# Revit family: STS-504_RV17_LOD400 (05.11.23)
name_source: partatom
category: Электрооборудование
revit_build: Autodesk Revit 2017 (Build: 20170118_1100(x64)
units: mm (PartAtom-declared; Revit-internal decimal feet)

## family parameters
Всегда вертикально = Да
Конфигурация панели = Два столбца, слева направо
На основе рабочей плоскости = Нет
Общий = Нет
При загрузке вырезать с полостями = Нет
Размер круглого соединителя = Использовать диаметр
Тип детали = Щит
Точка расчета площади = Нет

## types (1)
- STS-504
    ADSK_URL страницы изделия = https://stilsoft.ru
    ADSK_Единица измерения = шт.
    ADSK_Завод-изготовитель = ООО «Основа Безопасности»
    ADSK_Количество = 1
    ADSK_Марка = СТВФ.426471.287
    ADSK_Масса = 12
    ADSK_Наименование = Контроллер STS-504
    ADSK_Размер_Высота = 560 мм
    ADSK_Размер_Глубина = 257 мм
    ADSK_Размер_Ширина = 400 мм
    d_короба = 20 мм
    Вариант исполнения = уличный
    Включение вентиляции при температуре, от, °С = 35
    Диапазон рабочих температур, °С = от –40 до +50
    Конфигуратор контроллера STS-504 = https://stilsoft.ru
    Напряжение = 220
    Напряжение электропитания переменного тока, В/Гц = 220/50
    Напряжение электропитания постоянного тока вентилятора, В = 12
    Номинальный ток автоматического выключателя напряжения питания, А = 25 А
